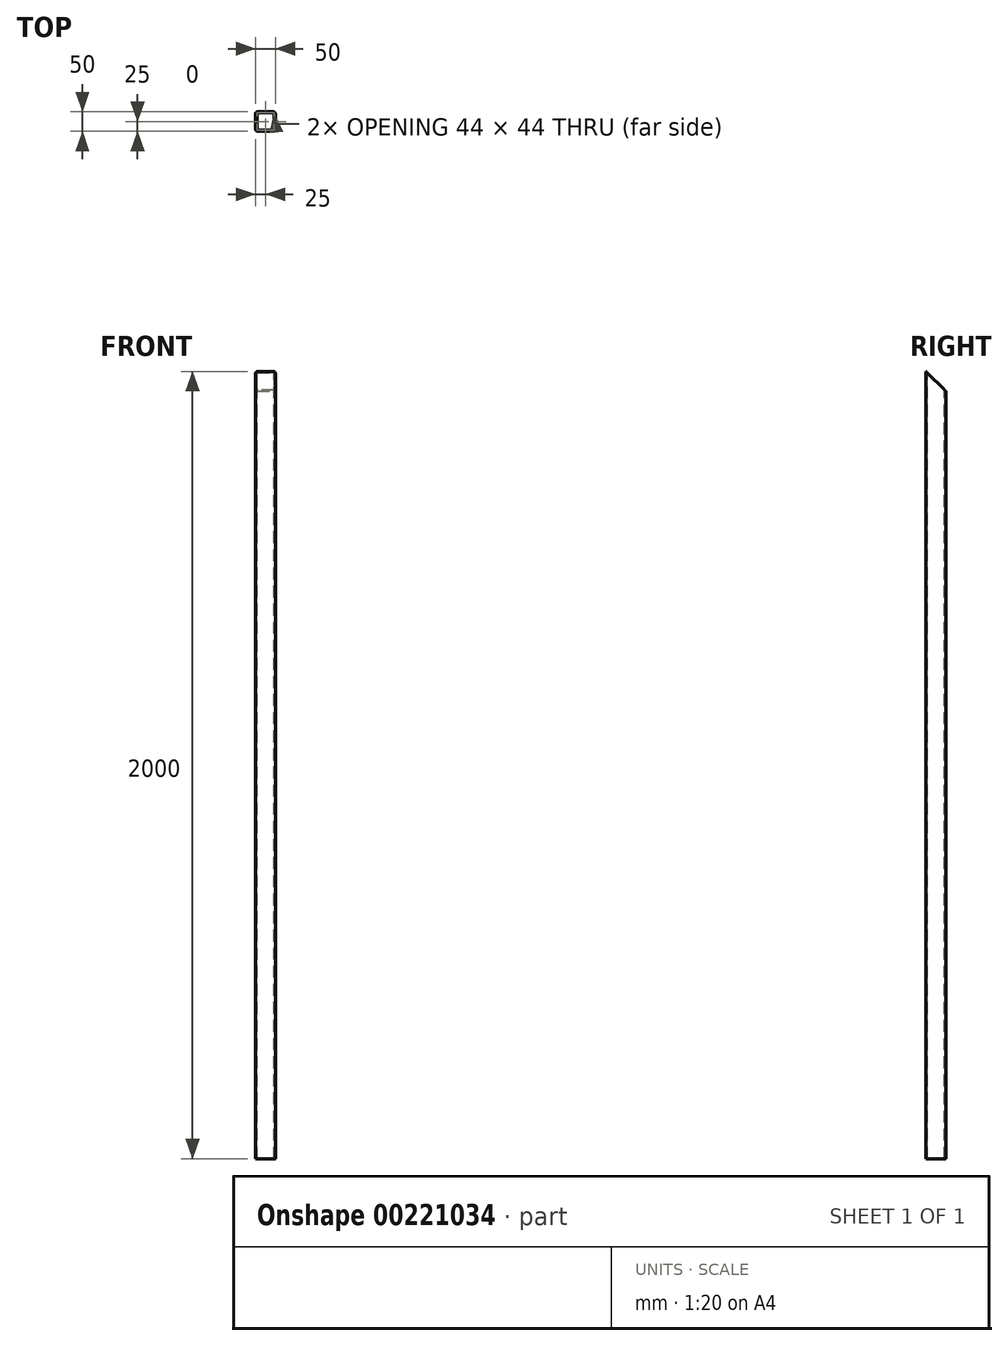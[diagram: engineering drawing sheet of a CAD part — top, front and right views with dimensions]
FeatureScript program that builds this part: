
annotation { "Feature Type Name" : "Feature", "Feature Type Description" : "" }
export const myFeature = defineFeature(function(context is Context, id is Id, definition is map)
    precondition{}
    {
        {
            var Q0;
            Q0=qCreatedBy(makeId("Top.planeOp"),FACE);
            var sketch = newSketch(context, id + "F0", { "sketchPlane" : qUnion([Q0])});
            skLineSegment(sketch, "E0.bottom", {"start": v(20, 25) * mm, "end": v(-20, 25) * mm});
            skLineSegment(sketch, "E0.top", {"start": v(20, -25) * mm, "end": v(-20, -25) * mm});
            skLineSegment(sketch, "E0.left", {"start": v(25, 20) * mm, "end": v(25, -20) * mm});
            skLineSegment(sketch, "E0.right", {"start": v(-25, 20) * mm, "end": v(-25, -20) * mm});
            skPoint(sketch, "E0.middle", {"position": v(0, 0) * mm});
            skPoint(sketch, "E1.visualSharp", {"position": v(25, -25) * mm});
            skArc(sketch, "E1.filletArc", {"start": v(20, -25) * mm, "mid": v(23.54, -23.54) * mm, "end": v(25, -20) * mm});
            skPoint(sketch, "E2.visualSharp", {"position": v(-25, -25) * mm});
            skArc(sketch, "E2.filletArc", {"start": v(-25, -20) * mm, "mid": v(-23.54, -23.54) * mm, "end": v(-20, -25) * mm});
            skPoint(sketch, "E3.visualSharp", {"position": v(-25, 25) * mm});
            skArc(sketch, "E3.filletArc", {"start": v(-20, 25) * mm, "mid": v(-23.54, 23.54) * mm, "end": v(-25, 20) * mm});
            skPoint(sketch, "E4.visualSharp", {"position": v(25, 25) * mm});
            skArc(sketch, "E4.filletArc", {"start": v(25, 20) * mm, "mid": v(23.54, 23.54) * mm, "end": v(20, 25) * mm});
            skSolve(sketch);
        }
        {
            var Q0;
            Q0=makeQuery(id+"F0.imprint","IMPRINT",FACE,{"disambiguationData":[TD([[makeQuery(id+"F0.imprint","IMPRINT",EDGE,{"derivedFrom":sQuery(id+"F0.wireOp",EDGE,"E0.bottom")}),1.0]])]});
            extrude(context, id + "F1", {"entities" : qUnion([Q0]), "endBound" : BoundingType.SYMMETRIC, "depth" : 2000 * mm, "hasSecondDirection" : true, "secondDirectionOppositeDirection" : true, "secondDirectionDepth" : 1000 * mm});
        }
        {
            var Q0;
            Q0=makeQuery(id+"F1.opExtrude","CAP_FACE",FACE,{"disambiguationData":[OSD([sQuery(id+"F0.wireOp",EDGE,"E0.bottom"),sQuery(id+"F0.wireOp",EDGE,"E0.top"),sQuery(id+"F0.wireOp",EDGE,"E0.left"),sQuery(id+"F0.wireOp",EDGE,"E0.right"),sQuery(id+"F0.wireOp",EDGE,"E1.filletArc"),sQuery(id+"F0.wireOp",EDGE,"E2.filletArc"),sQuery(id+"F0.wireOp",EDGE,"E3.filletArc"),sQuery(id+"F0.wireOp",EDGE,"E4.filletArc")])],"isStart":false});
            var sketch = newSketch(context, id + "F2", { "sketchPlane" : qUnion([Q0])});
            skLineSegment(sketch, "E5.0", {"start": v(-20, -22) * mm, "end": v(20, -22) * mm});
            skLineSegment(sketch, "E5.1", {"start": v(-22, 20) * mm, "end": v(-22, -20) * mm});
            skLineSegment(sketch, "E5.2", {"start": v(20, 22) * mm, "end": v(-20, 22) * mm});
            skLineSegment(sketch, "E5.3", {"start": v(22, -20) * mm, "end": v(22, 20) * mm});
            skPoint(sketch, "E6.visualSharp", {"position": v(-22, -22) * mm});
            skArc(sketch, "E6.filletArc", {"start": v(-22, -20) * mm, "mid": v(-21.41, -21.41) * mm, "end": v(-20, -22) * mm});
            skPoint(sketch, "E7.visualSharp", {"position": v(22, -22) * mm});
            skArc(sketch, "E7.filletArc", {"start": v(20, -22) * mm, "mid": v(21.41, -21.41) * mm, "end": v(22, -20) * mm});
            skPoint(sketch, "E8.visualSharp", {"position": v(22, 22) * mm});
            skArc(sketch, "E8.filletArc", {"start": v(22, 20) * mm, "mid": v(21.41, 21.41) * mm, "end": v(20, 22) * mm});
            skPoint(sketch, "E9.visualSharp", {"position": v(-22, 22) * mm});
            skArc(sketch, "E9.filletArc", {"start": v(-20, 22) * mm, "mid": v(-21.41, 21.41) * mm, "end": v(-22, 20) * mm});
            skSolve(sketch);
        }
        {
            var Q0;
            Q0=makeQuery(id+"F2.imprint","IMPRINT",FACE,{"disambiguationData":[TD([[makeQuery(id+"F2.imprint","IMPRINT",EDGE,{"derivedFrom":sQuery(id+"F2.wireOp",EDGE,"E5.0")}),1.0]])]});
            extrude(context, id + "F3", {"entities" : qUnion([Q0]), "operationType" : NewBodyOperationType.REMOVE, "endBound" : BoundingType.THROUGH_ALL, "oppositeDirection" : true, "depth" : 25 * mm});
        }
        {
            var Q0;
            Q0=qCreatedBy(makeId("Right.planeOp"),FACE);
            var sketch = newSketch(context, id + "F4", { "sketchPlane" : qUnion([Q0])});
            skLineSegment(sketch, "E10", {"start": v(-25, 1000) * mm, "end": v(25, 950) * mm});
            skLineSegment(sketch, "E11", {"start": v(25, 950) * mm, "end": v(25, 1000) * mm});
            skLineSegment(sketch, "E12", {"start": v(25, 1000) * mm, "end": v(-25, 1000) * mm});
            skSolve(sketch);
        }
        {
            var Q0;
            Q0 = qSketchRegion(id + "F4", true);
            extrude(context, id + "F5", {"entities" : qUnion([Q0]), "operationType" : NewBodyOperationType.REMOVE, "endBound" : BoundingType.THROUGH_ALL, "oppositeDirection" : true, "depth" : 25 * mm, "hasSecondDirection" : true, "secondDirectionOppositeDirection" : false, "secondDirectionDepth" : 25 * mm});
        }
    });
